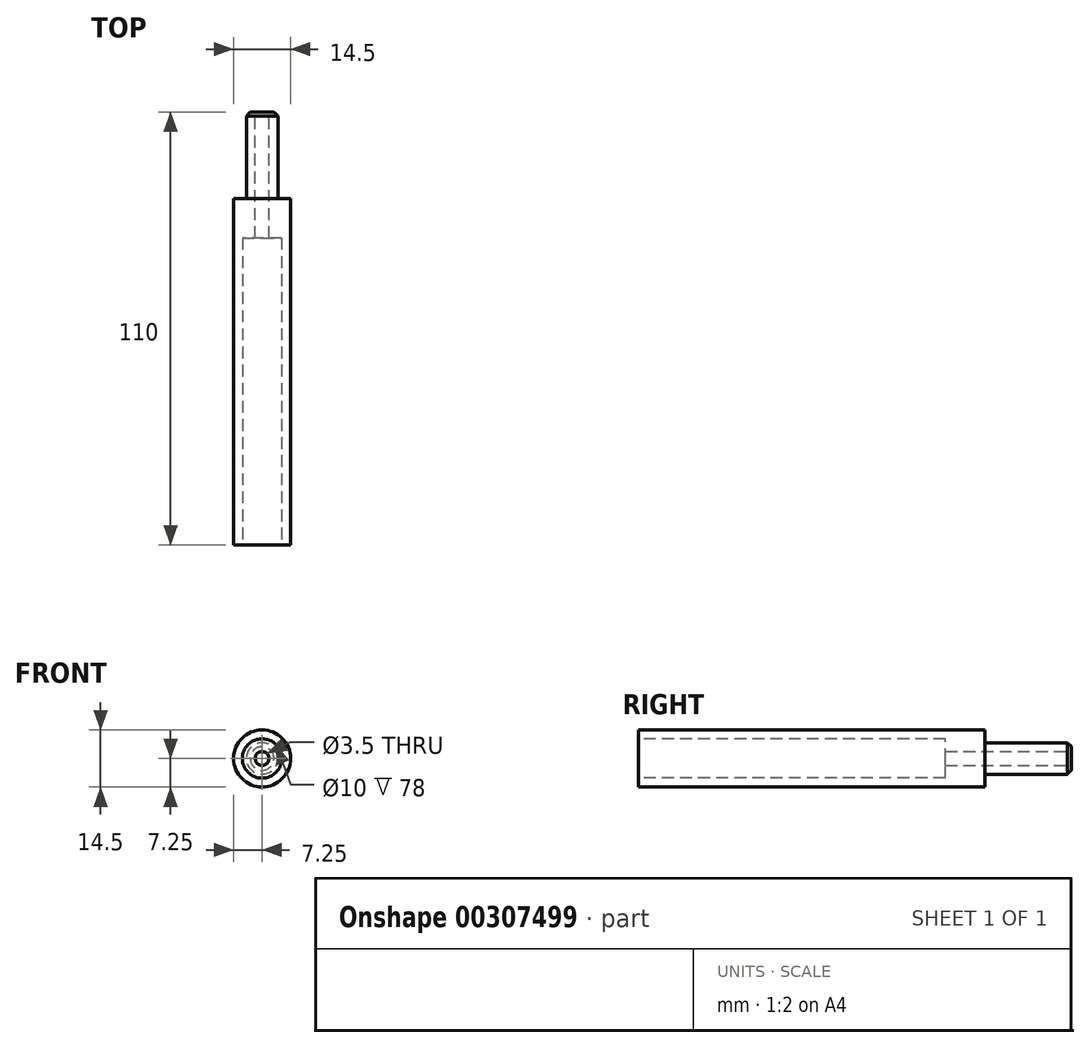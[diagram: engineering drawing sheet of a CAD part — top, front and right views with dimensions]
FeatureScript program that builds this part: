
annotation { "Feature Type Name" : "Feature", "Feature Type Description" : "" }
export const myFeature = defineFeature(function(context is Context, id is Id, definition is map)
    precondition{}
    {
        {
            var Q0;
            Q0=qCreatedBy(makeId("Front.planeOp"),FACE);
            var sketch = newSketch(context, id + "F0", { "sketchPlane" : qUnion([Q0])});
            skCircle(sketch, "E0", {"center": v(0, 0) * mm, "radius": 7.25 * mm});
            skSolve(sketch);
        }
        {
            var Q0;
            Q0 = qSketchRegion(id + "F0", true);
            extrude(context, id + "F1", {"entities" : qUnion([Q0]), "depth" : 88 * mm});
        }
        {
            var Q0;
            Q0=qCreatedBy(makeId("Front.planeOp"),FACE);
            var sketch = newSketch(context, id + "F2", { "sketchPlane" : qUnion([Q0])});
            skCircle(sketch, "E1", {"center": v(0, 0) * mm, "radius": 4 * mm});
            skSolve(sketch);
        }
        {
            var Q0;
            Q0 = qSketchRegion(id + "F2", true);
            extrude(context, id + "F3", {"entities" : qUnion([Q0]), "operationType" : NewBodyOperationType.ADD, "oppositeDirection" : true, "depth" : 22 * mm});
        }
        {
            var Q0;
            Q0=makeQuery(id+"F3.opExtrude","CAP_EDGE",EDGE,{"disambiguationData":[OSD([sQuery(id+"F2.wireOp",EDGE,"E1")])],"isStart":false});
            chamfer(context, id + "F4", {"entities" : qUnion([Q0]), "width" : 1 * mm, "tangentPropagation" : true});
        }
        {
            var Q0;
            Q0=makeQuery(id+"F3.opExtrude","CAP_FACE",FACE,{"disambiguationData":[OSD([sQuery(id+"F2.wireOp",EDGE,"E1")])],"isStart":false});
            var sketch = newSketch(context, id + "F5", { "sketchPlane" : qUnion([Q0])});
            skCircle(sketch, "E2", {"center": v(0, 0) * mm, "radius": 1.75 * mm});
            skSolve(sketch);
        }
        {
            var Q0;
            Q0 = qSketchRegion(id + "F5", true);
            extrude(context, id + "F6", {"entities" : qUnion([Q0]), "operationType" : NewBodyOperationType.REMOVE, "oppositeDirection" : true, "depth" : 120 * mm});
        }
        {
            var Q0;
            Q0=makeQuery(id+"F1.opExtrude","CAP_FACE",FACE,{"disambiguationData":[OSD([sQuery(id+"F0.wireOp",EDGE,"E0")])],"isStart":false});
            var sketch = newSketch(context, id + "F7", { "sketchPlane" : qUnion([Q0])});
            skCircle(sketch, "E3", {"center": v(0, 0) * mm, "radius": 5 * mm});
            skSolve(sketch);
        }
        {
            var Q0;
            Q0 = qSketchRegion(id + "F7", true);
            extrude(context, id + "F8", {"entities" : qUnion([Q0]), "operationType" : NewBodyOperationType.REMOVE, "oppositeDirection" : true, "depth" : 78 * mm});
        }
    });
